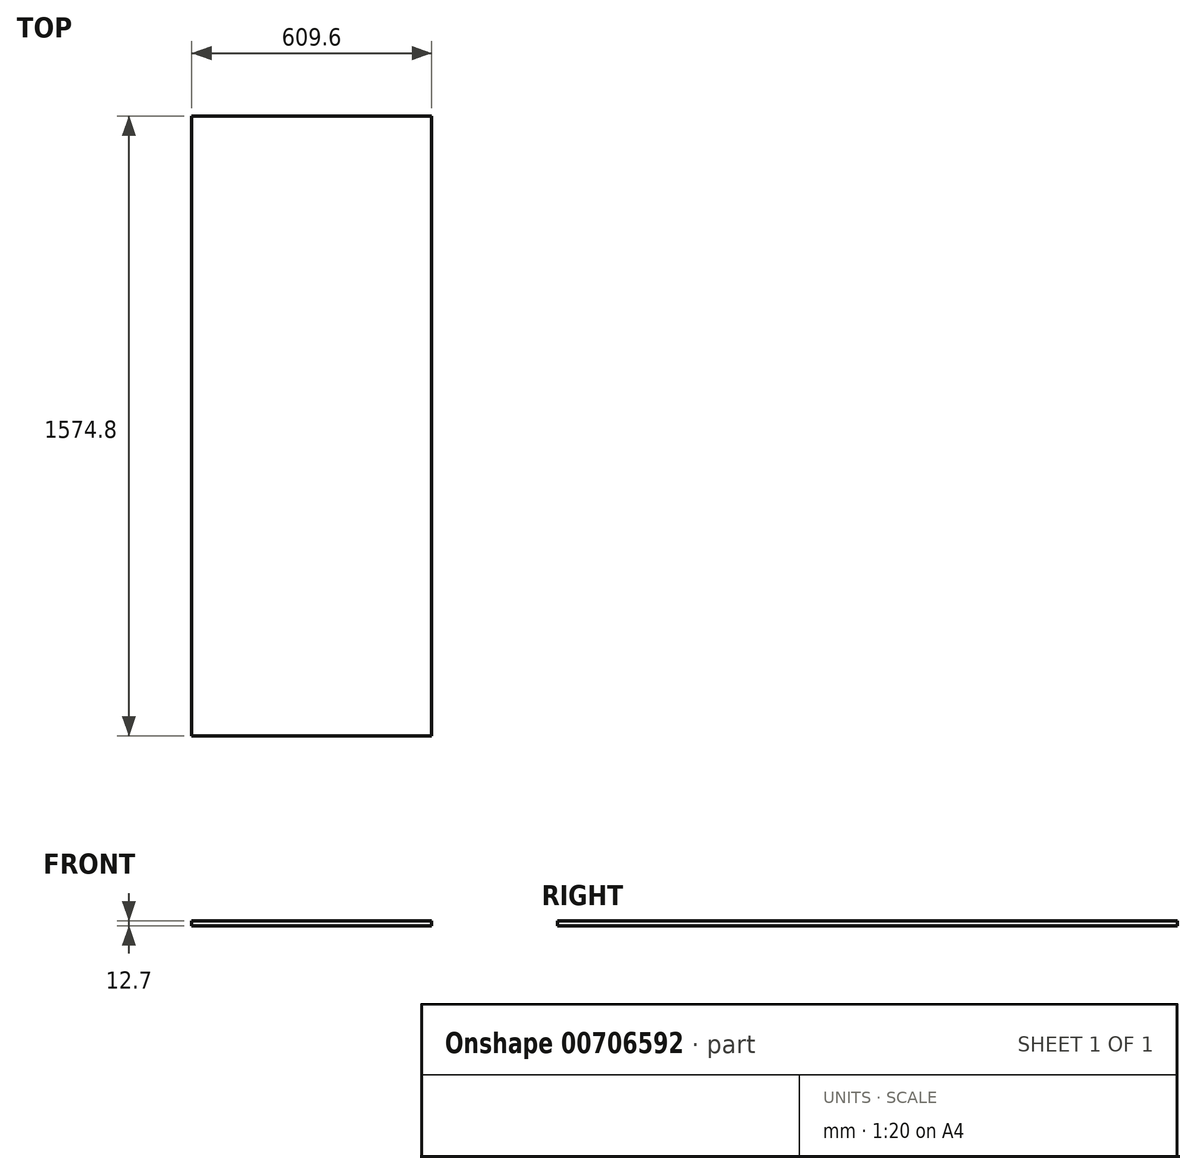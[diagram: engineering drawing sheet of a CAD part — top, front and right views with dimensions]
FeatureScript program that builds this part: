
annotation { "Feature Type Name" : "Feature", "Feature Type Description" : "" }
export const myFeature = defineFeature(function(context is Context, id is Id, definition is map)
    precondition{}
    {
        {
            var Q0;
            Q0=qCreatedBy(makeId("Top.planeOp"),FACE);
            var sketch = newSketch(context, id + "F0", { "sketchPlane" : qUnion([Q0])});
            skLineSegment(sketch, "E0.bottom", {"start": v(-304.8, -787.4) * mm, "end": v(304.8, -787.4) * mm});
            skLineSegment(sketch, "E0.top", {"start": v(-304.8, 787.4) * mm, "end": v(304.8, 787.4) * mm});
            skLineSegment(sketch, "E0.left", {"start": v(-304.8, -787.4) * mm, "end": v(-304.8, 787.4) * mm});
            skLineSegment(sketch, "E0.right", {"start": v(304.8, -787.4) * mm, "end": v(304.8, 787.4) * mm});
            skPoint(sketch, "E0.middle", {"position": v(0, 0) * mm});
            skSolve(sketch);
        }
        {
            var Q0;
            Q0 = qSketchRegion(id + "F0", true);
            extrude(context, id + "F1", {"entities" : qUnion([Q0]), "depth" : 12.7 * mm, "offsetDistance" : 25.4 * mm});
        }
    });
